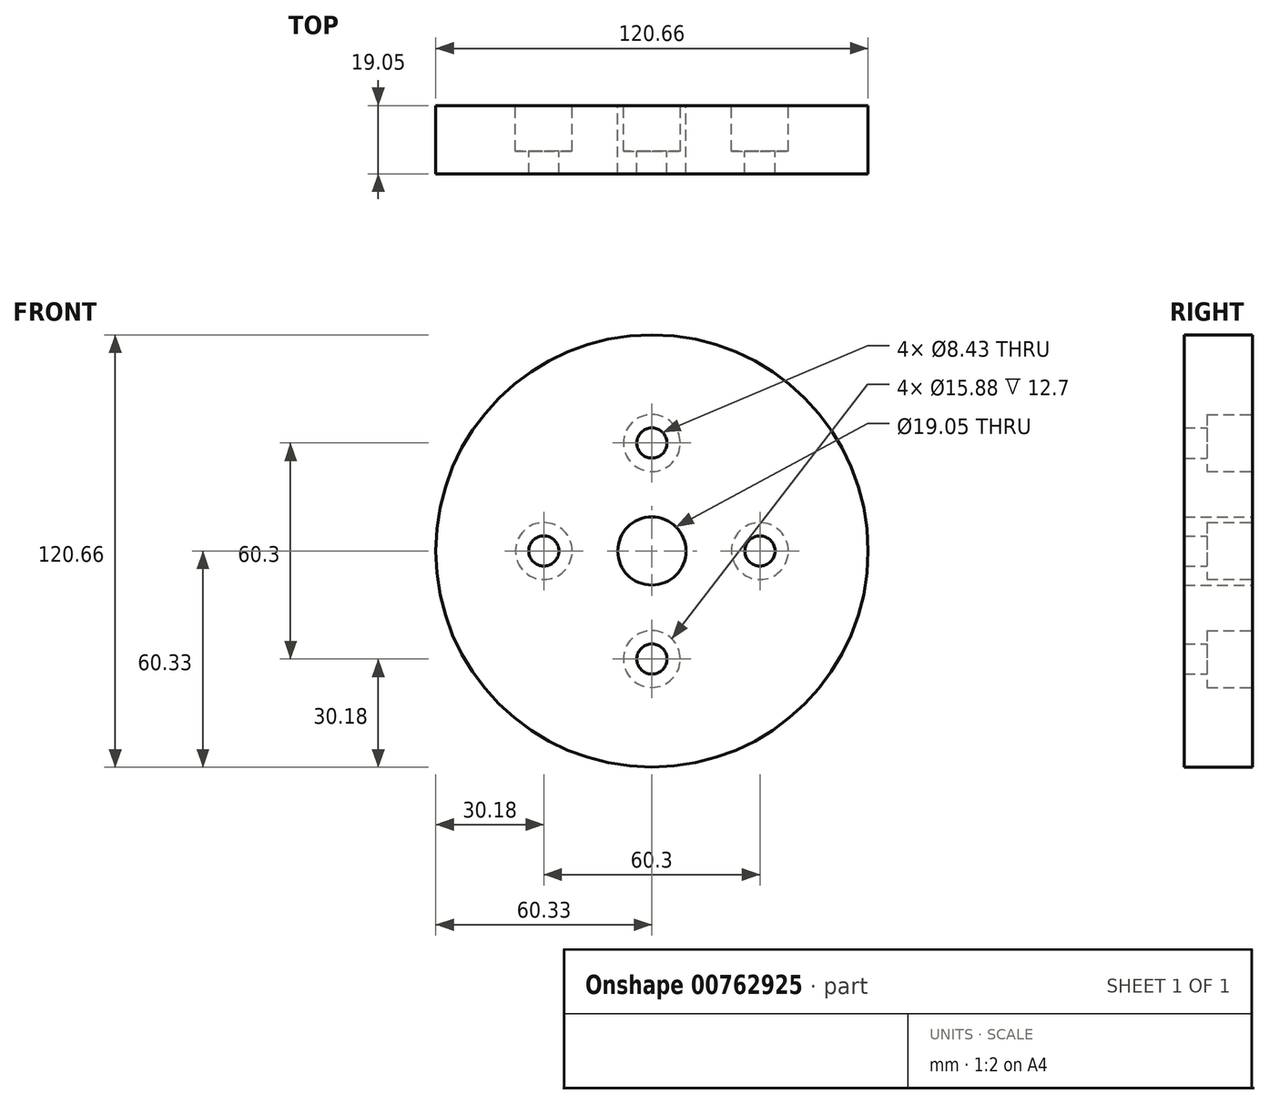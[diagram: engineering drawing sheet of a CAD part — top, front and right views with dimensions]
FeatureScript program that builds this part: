
annotation { "Feature Type Name" : "Feature", "Feature Type Description" : "" }
export const myFeature = defineFeature(function(context is Context, id is Id, definition is map)
    precondition{}
    {
        {
            var Q0;
            Q0=qCreatedBy(makeId("Front.planeOp"),FACE);
            var sketch = newSketch(context, id + "F0", { "sketchPlane" : qUnion([Q0])});
            skCircle(sketch, "E0", {"center": v(0, 0) * mm, "radius": 60.33 * mm});
            skSolve(sketch);
        }
        {
            var Q0;
            Q0=makeQuery(id+"F0.imprint","IMPRINT",FACE,{"disambiguationData":[TD([[makeQuery(id+"F0.imprint","IMPRINT",EDGE,{"derivedFrom":sQuery(id+"F0.wireOp",EDGE,"E0")}),1.0]])]});
            extrude(context, id + "F1", {"entities" : qUnion([Q0]), "oppositeDirection" : true, "depth" : 19.05 * mm, "offsetDistance" : 25.4 * mm});
        }
        {
            var Q0;
            Q0=makeQuery(id+"F1.opExtrude","CAP_FACE",FACE,{"disambiguationData":[OSD([sQuery(id+"F0.wireOp",EDGE,"E0")])],"isStart":false});
            var sketch = newSketch(context, id + "F2", { "sketchPlane" : qUnion([Q0])});
            skPoint(sketch, "E1", {"position": v(0, 30.15) * mm});
            skPoint(sketch, "E2", {"position": v(30.15, 0) * mm});
            skPoint(sketch, "E3", {"position": v(0, -30.15) * mm});
            skPoint(sketch, "E4", {"position": v(-30.15, 0) * mm});
            skSolve(sketch);
        }
        {
            var Q0;
            Q0=sQuery(id+"F2.wireOp",VERTEX,"E1");
            var Q1;
            Q1=sQuery(id+"F2.wireOp",VERTEX,"E2");
            var Q2;
            Q2=sQuery(id+"F2.wireOp",VERTEX,"E3");
            var Q3;
            Q3=sQuery(id+"F2.wireOp",VERTEX,"E4");
            var Q4;
            Q4=makeQuery(id+"F1.opExtrude","SWEPT_BODY",BODY,{"disambiguationData":[OSD([sQuery(id+"F0.wireOp",EDGE,"E0")])]});
            hole(context, id + "F3", {"style" : HoleStyle.C_BORE, "endStyle" : HoleEndStyle.THROUGH, "holeDiameter" : 8.43 * mm, "cBoreDiameter" : 15.88 * mm, "cBoreDepth" : 12.7 * mm, "majorDiameter" : 6.35 * mm, "tappedDepth" : 110.49 * mm, "tapClearance" : 3, "startFromSketch" : true, "locations" : qUnion([Q0, Q1, Q2, Q3]), "scope" : qUnion([Q4])});
        }
        {
            var Q0;
            Q0=makeQuery(id+"F1.opExtrude","CAP_FACE",FACE,{"disambiguationData":[OSD([sQuery(id+"F0.wireOp",EDGE,"E0")])],"isStart":false});
            var sketch = newSketch(context, id + "F4", { "sketchPlane" : qUnion([Q0])});
            skCircle(sketch, "E5", {"center": v(0, 0) * mm, "radius": 9.53 * mm});
            skSolve(sketch);
        }
        {
            var Q0;
            Q0=makeQuery(id+"F4.imprint","IMPRINT",FACE,{"disambiguationData":[TD([[makeQuery(id+"F4.imprint","IMPRINT",EDGE,{"derivedFrom":sQuery(id+"F4.wireOp",EDGE,"E5")}),1.0]])]});
            var Q1;
            Q1=sQuery(id+"F4.wireOp",EDGE,"E5");
            extrude(context, id + "F5", {"entities" : qUnion([Q0]), "operationType" : NewBodyOperationType.REMOVE, "surfaceEntities" : qUnion([Q1]), "oppositeDirection" : true, "depth" : 25.4 * mm, "offsetDistance" : 25.4 * mm});
        }
    });
